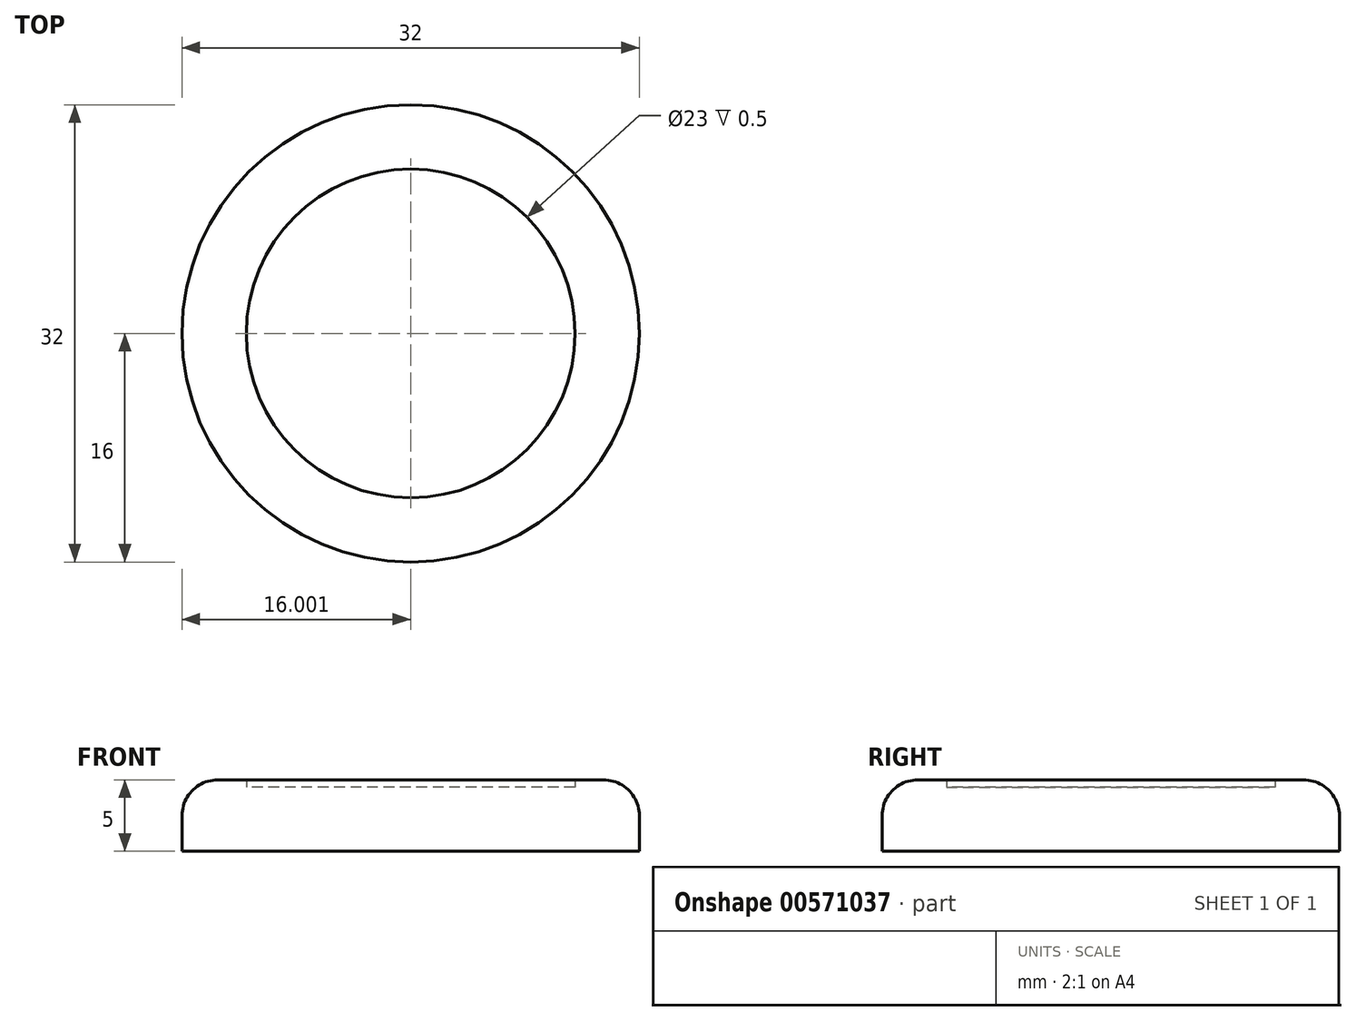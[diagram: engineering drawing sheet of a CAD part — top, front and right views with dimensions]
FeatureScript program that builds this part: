
annotation { "Feature Type Name" : "Feature", "Feature Type Description" : "" }
export const myFeature = defineFeature(function(context is Context, id is Id, definition is map)
    precondition{}
    {
        {
            var Q0;
            Q0=qCreatedBy(makeId("Top.planeOp"),FACE);
            var sketch = newSketch(context, id + "F0", { "sketchPlane" : qUnion([Q0])});
            skCircle(sketch, "E0", {"center": v(-13.78, 0) * mm, "radius": 16 * mm});
            skSolve(sketch);
        }
        {
            var Q0;
            Q0=makeQuery(id+"F0.imprint","IMPRINT",FACE,{"disambiguationData":[TD([[makeQuery(id+"F0.imprint","IMPRINT",EDGE,{"derivedFrom":sQuery(id+"F0.wireOp",EDGE,"E0")}),1.0]])]});
            extrude(context, id + "F1", {"entities" : qUnion([Q0]), "depth" : 5 * mm, "offsetDistance" : 25 * mm});
        }
        {
            var Q0;
            Q0=makeQuery(id+"F1.opExtrude","CAP_FACE",FACE,{"disambiguationData":[OSD([sQuery(id+"F0.wireOp",EDGE,"E0")])],"isStart":false});
            shell(context, id + "F2", {"entities" : qUnion([Q0]), "thickness" : 4.5 * mm});
        }
        {
            var Q0;
            Q0=makeQuery(id+"F1.opExtrude","CAP_EDGE",EDGE,{"disambiguationData":[OSD([sQuery(id+"F0.wireOp",EDGE,"E0")])],"isStart":false});
            fillet(context, id + "F3", {"entities" : qUnion([Q0]), "radius" : 2.5 * mm, "tangentPropagation" : true, "allowEdgeOverflow" : false});
        }
    });
